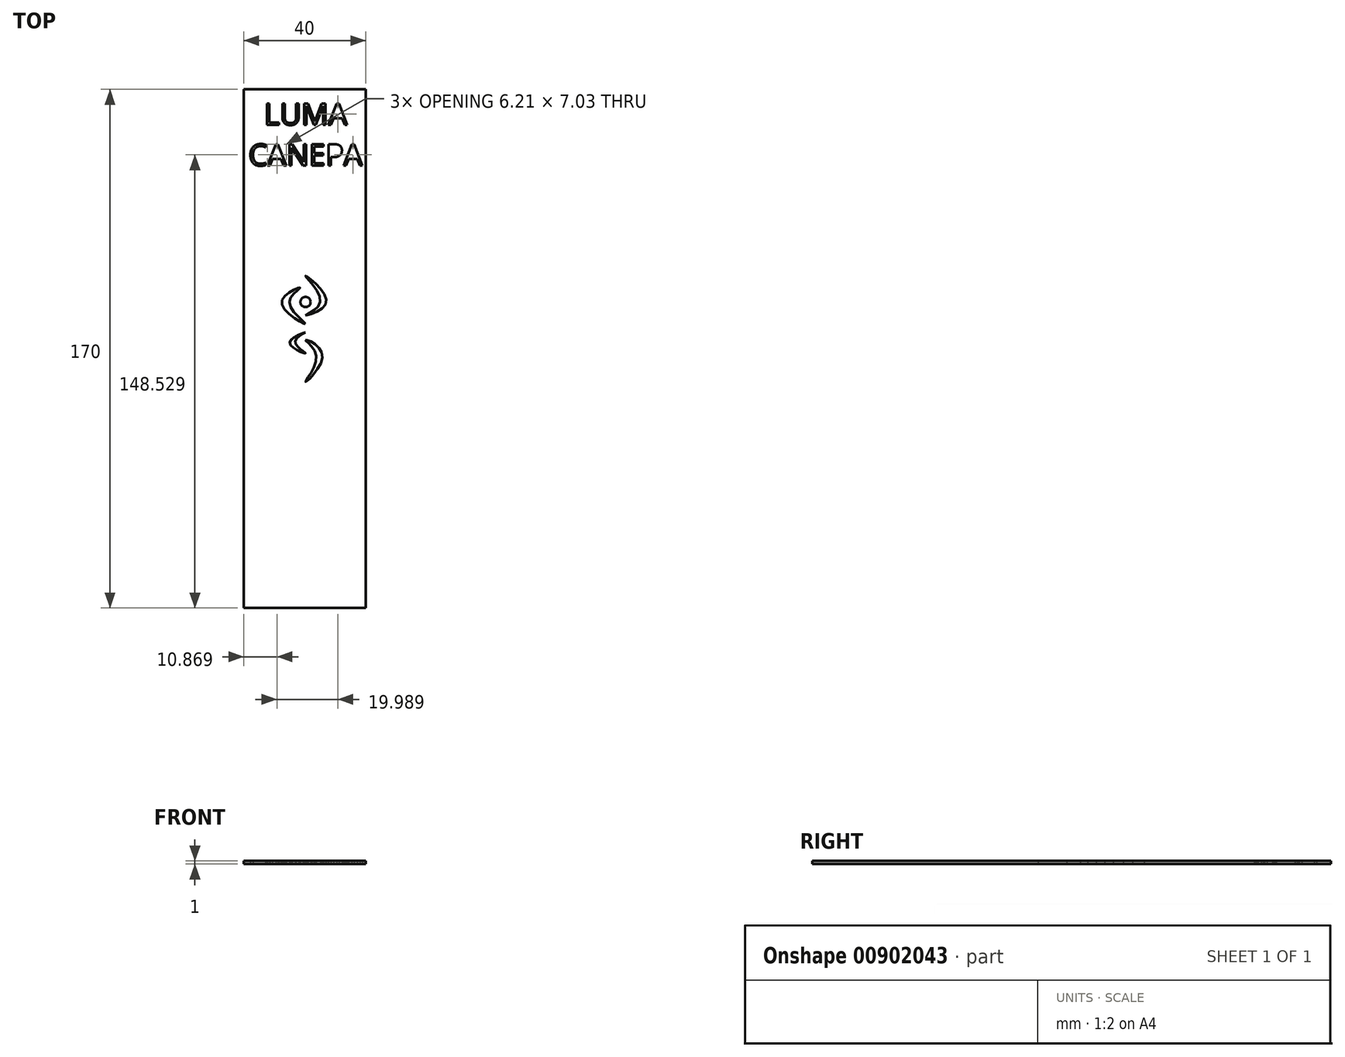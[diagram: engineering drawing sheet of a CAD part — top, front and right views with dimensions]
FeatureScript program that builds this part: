
annotation { "Feature Type Name" : "Feature", "Feature Type Description" : "" }
export const myFeature = defineFeature(function(context is Context, id is Id, definition is map)
    precondition{}
    {
        {
            var Q0;
            Q0=qCreatedBy(makeId("Top.planeOp"),FACE);
            var sketch = newSketch(context, id + "F0", { "sketchPlane" : qUnion([Q0])});
            skLineSegment(sketch, "E0.bottom", {"start": v(-20.26, 104.78) * mm, "end": v(19.74, 104.78) * mm});
            skLineSegment(sketch, "E0.top", {"start": v(-20.26, -65.22) * mm, "end": v(19.74, -65.22) * mm});
            skLineSegment(sketch, "E0.left", {"start": v(-20.26, 104.78) * mm, "end": v(-20.26, -65.22) * mm});
            skLineSegment(sketch, "E0.right", {"start": v(19.74, 104.78) * mm, "end": v(19.74, -65.22) * mm});
            skText(sketch, "E1", { "text": "  LUMA\nCANEPA", "fontName": "OpenSans-Regular.ttf"});
            skCircle(sketch, "E2", {"center": v(0, 35.06) * mm, "radius": 1.66 * mm});
            skFitSpline(sketch, "E3", {"points": [v(0, 25.1) * mm, v(-3.4, 22.08) * mm, v(0, 18.27) * mm, v(-5.16, 21.68) * mm, v(0, 25.1) * mm]});
            skFitSpline(sketch, "E4", {"points": [v(0, 22.68) * mm, v(3.47, 17.36) * mm, v(0, 8.87) * mm, v(5.52, 17.84) * mm, v(0, 22.68) * mm]});
            skFitSpline(sketch, "E5", {"points": [v(0, 30.65) * mm, v(4.8, 35.06) * mm, v(0, 43.62) * mm, v(6.8, 35.06) * mm, v(0, 30.65) * mm]});
            skFitSpline(sketch, "E6", {"points": [v(0, 27.85) * mm, v(-5.3, 35.06) * mm, v(-1.74, 39.76) * mm, v(-7.86, 35.06) * mm, v(0, 27.85) * mm]});
            const initialGuessF0  = {"E1": [-0.01868, 0.09313, 1, 0, 0.00706]};
            skSetInitialGuess(sketch, initialGuessF0);
            skSolve(sketch);
        }
        {
            var Q0;
            Q0=makeQuery(id+"F0.imprint","IMPRINT",FACE,{"disambiguationData":[TD([[makeQuery(id+"F0.imprint","IMPRINT",EDGE,{"derivedFrom":sQuery(id+"F0.wireOp",EDGE,"E0.bottom")}),-1.0]])]});
            extrude(context, id + "F1", {"entities" : qUnion([Q0]), "depth" : 1 * mm, "offsetDistance" : 25 * mm});
        }
    });
